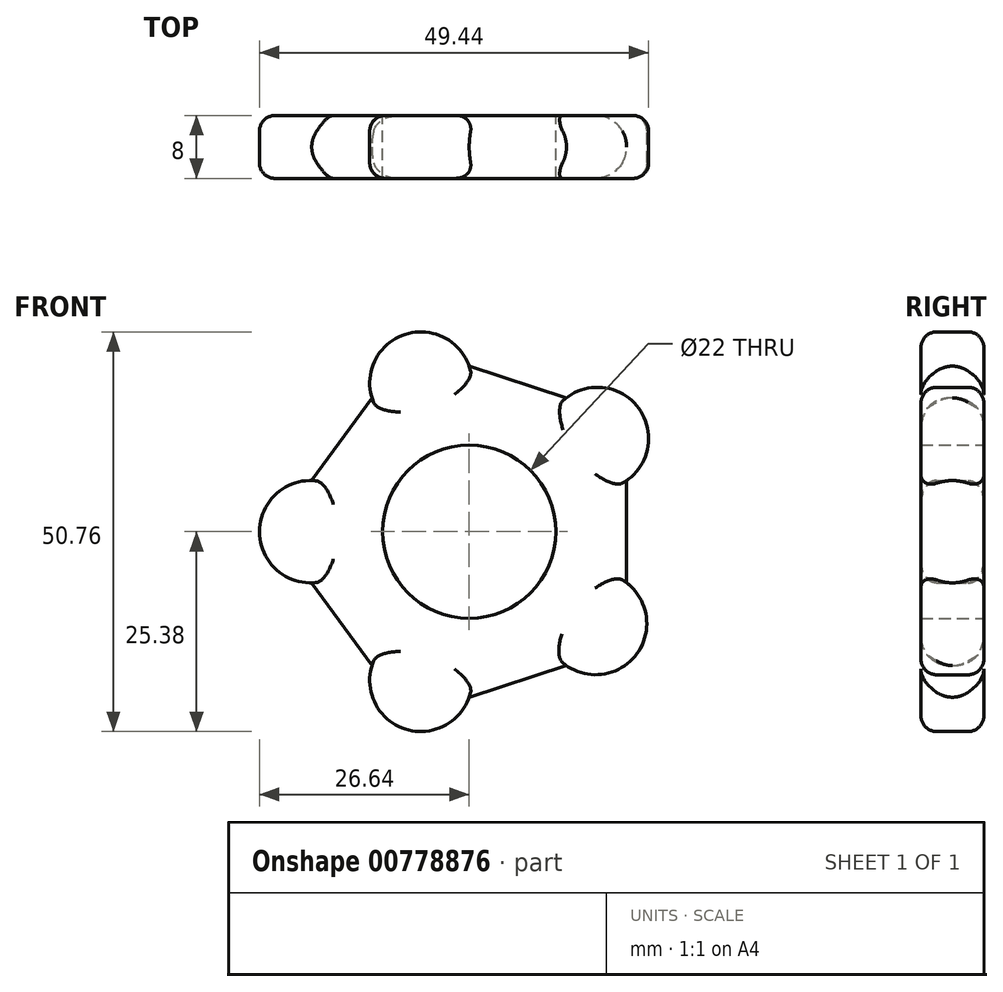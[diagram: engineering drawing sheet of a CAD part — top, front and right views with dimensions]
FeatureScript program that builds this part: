
annotation { "Feature Type Name" : "Feature", "Feature Type Description" : "" }
export const myFeature = defineFeature(function(context is Context, id is Id, definition is map)
    precondition{}
    {
        {
            var Q0;
            Q0=qCreatedBy(makeId("Front.planeOp"),FACE);
            var sketch = newSketch(context, id + "F0", { "sketchPlane" : qUnion([Q0])});
            skCircle(sketch, "E0.cCircle", {"center": v(0, 0) * mm, "radius": 20 * mm, "construction": true});
            skLineSegment(sketch, "E0.0", {"start": v(20, 6.5) * mm, "end": v(20, -6.5) * mm});
            skLineSegment(sketch, "E0.1", {"start": v(20, -6.5) * mm, "end": v(12.36, -17.01) * mm});
            skLineSegment(sketch, "E0.2", {"start": v(12.36, -17.01) * mm, "end": v(0, -21.03) * mm});
            skLineSegment(sketch, "E0.3", {"start": v(0, -21.03) * mm, "end": v(-12.36, -17.01) * mm});
            skLineSegment(sketch, "E0.4", {"start": v(-12.36, -17.01) * mm, "end": v(-20, -6.5) * mm});
            skLineSegment(sketch, "E0.5", {"start": v(-20, -6.5) * mm, "end": v(-20, 6.5) * mm});
            skLineSegment(sketch, "E0.6", {"start": v(-20, 6.5) * mm, "end": v(-12.36, 17.01) * mm});
            skLineSegment(sketch, "E0.7", {"start": v(-12.36, 17.01) * mm, "end": v(0, 21.03) * mm});
            skLineSegment(sketch, "E0.8", {"start": v(0, 21.03) * mm, "end": v(12.36, 17.01) * mm});
            skLineSegment(sketch, "E0.9", {"start": v(12.36, 17.01) * mm, "end": v(20, 6.5) * mm});
            skPoint(sketch, "E0.0.midPoint", {"position": v(20, 0) * mm});
            skCircle(sketch, "E1", {"center": v(0, 0) * mm, "radius": 11 * mm});
            skArc(sketch, "E2", {"start": v(20, 6.5) * mm, "mid": v(21.56, 15.66) * mm, "end": v(12.36, 17.01) * mm});
            skArc(sketch, "E3", {"start": v(12.36, -17.01) * mm, "mid": v(21.32, -15.5) * mm, "end": v(20, -6.5) * mm});
            skArc(sketch, "E4", {"start": v(-12.36, -17.01) * mm, "mid": v(-8.14, -25.07) * mm, "end": v(0, -21.03) * mm});
            skArc(sketch, "E5", {"start": v(-20, 6.5) * mm, "mid": v(-26.64, 0) * mm, "end": v(-20, -6.5) * mm});
            skArc(sketch, "E6", {"start": v(0, 21.03) * mm, "mid": v(-8.14, 25.07) * mm, "end": v(-12.36, 17.01) * mm});
            skSolve(sketch);
        }
        {
            var Q0;
            Q0=makeQuery(id+"F0.imprint","IMPRINT",FACE,{"disambiguationData":[TD([[makeQuery(id+"F0.imprint","IMPRINT",EDGE,{"derivedFrom":sQuery(id+"F0.wireOp",EDGE,"E0.0")}),-1.0]])]});
            var Q1;
            Q1=makeQuery(id+"F0.imprint","IMPRINT",FACE,{"disambiguationData":[TD([[makeQuery(id+"F0.imprint","IMPRINT",EDGE,{"derivedFrom":sQuery(id+"F0.wireOp",EDGE,"E0.1")}),1.0]])]});
            var Q2;
            Q2=makeQuery(id+"F0.imprint","IMPRINT",FACE,{"disambiguationData":[TD([[makeQuery(id+"F0.imprint","IMPRINT",EDGE,{"derivedFrom":sQuery(id+"F0.wireOp",EDGE,"E0.3")}),1.0]])]});
            var Q3;
            Q3=makeQuery(id+"F0.imprint","IMPRINT",FACE,{"disambiguationData":[TD([[makeQuery(id+"F0.imprint","IMPRINT",EDGE,{"derivedFrom":sQuery(id+"F0.wireOp",EDGE,"E0.5")}),1.0]])]});
            var Q4;
            {var subQ0=sQuery(id+"F0.wireOp",EDGE,"E0.7");Q4=makeQuery(id+"F0.imprint","IMPRINT",FACE,{"disambiguationData":[TD([[makeQuery(id+"F0.imprint","IMPRINT",EDGE,{"derivedFrom":subQ0}),1.0]])]});}
            var Q5;
            Q5=makeQuery(id+"F0.imprint","IMPRINT",FACE,{"disambiguationData":[TD([[makeQuery(id+"F0.imprint","IMPRINT",EDGE,{"derivedFrom":sQuery(id+"F0.wireOp",EDGE,"E0.9")}),1.0]])]});
            extrude(context, id + "F1", {"entities" : qUnion([Q0, Q1, Q2, Q3, Q4, Q5]), "depth" : 8 * mm, "offsetDistance" : 25 * mm});
        }
        {
            var Q0;
            Q0=makeQuery(id+"F1.opExtrude","CAP_EDGE",EDGE,{"disambiguationData":[OSD([sQuery(id+"F0.wireOp",EDGE,"E0.8")])],"isStart":false});
            var Q1;
            Q1=makeQuery(id+"F1.opExtrude","CAP_EDGE",EDGE,{"disambiguationData":[OSD([sQuery(id+"F0.wireOp",EDGE,"E0.0")])],"isStart":false});
            var Q2;
            Q2=makeQuery(id+"F1.opExtrude","CAP_EDGE",EDGE,{"disambiguationData":[OSD([sQuery(id+"F0.wireOp",EDGE,"E0.2")])],"isStart":false});
            var Q3;
            Q3=makeQuery(id+"F1.opExtrude","CAP_EDGE",EDGE,{"disambiguationData":[OSD([sQuery(id+"F0.wireOp",EDGE,"E0.4")])],"isStart":false});
            var Q4;
            Q4=makeQuery(id+"F1.opExtrude","CAP_EDGE",EDGE,{"disambiguationData":[OSD([sQuery(id+"F0.wireOp",EDGE,"E0.6")])],"isStart":false});
            var Q5;
            Q5=makeQuery(id+"F1.opExtrude","CAP_EDGE",EDGE,{"disambiguationData":[OSD([sQuery(id+"F0.wireOp",EDGE,"E0.2")])],"isStart":true});
            var Q6;
            Q6=makeQuery(id+"F1.opExtrude","CAP_EDGE",EDGE,{"disambiguationData":[OSD([sQuery(id+"F0.wireOp",EDGE,"E0.4")])],"isStart":true});
            var Q7;
            Q7=makeQuery(id+"F1.opExtrude","CAP_EDGE",EDGE,{"disambiguationData":[OSD([sQuery(id+"F0.wireOp",EDGE,"E0.0")])],"isStart":true});
            var Q8;
            Q8=makeQuery(id+"F1.opExtrude","CAP_EDGE",EDGE,{"disambiguationData":[OSD([sQuery(id+"F0.wireOp",EDGE,"E0.8")])],"isStart":true});
            var Q9;
            Q9=makeQuery(id+"F1.opExtrude","CAP_EDGE",EDGE,{"disambiguationData":[OSD([sQuery(id+"F0.wireOp",EDGE,"E0.6")])],"isStart":true});
            fillet(context, id + "F2", {"entities" : qUnion([Q0, Q1, Q2, Q3, Q4, Q5, Q6, Q7, Q8, Q9]), "radius" : 4 * mm, "tangentPropagation" : true, "allowEdgeOverflow" : false});
        }
        {
            var Q0;
            Q0=makeQuery(id+"F1.opExtrude","CAP_EDGE",EDGE,{"disambiguationData":[OSD([sQuery(id+"F0.wireOp",EDGE,"E3")])],"isStart":false});
            var Q1;
            Q1=makeQuery(id+"F1.opExtrude","CAP_EDGE",EDGE,{"disambiguationData":[OSD([sQuery(id+"F0.wireOp",EDGE,"E4")])],"isStart":false});
            var Q2;
            Q2=makeQuery(id+"F1.opExtrude","CAP_EDGE",EDGE,{"disambiguationData":[OSD([sQuery(id+"F0.wireOp",EDGE,"E5")])],"isStart":false});
            var Q3;
            Q3=makeQuery(id+"F1.opExtrude","CAP_EDGE",EDGE,{"disambiguationData":[OSD([sQuery(id+"F0.wireOp",EDGE,"E6")])],"isStart":false});
            var Q4;
            Q4=makeQuery(id+"F1.opExtrude","CAP_EDGE",EDGE,{"disambiguationData":[OSD([sQuery(id+"F0.wireOp",EDGE,"E2")])],"isStart":false});
            fillet(context, id + "F3", {"entities" : qUnion([Q0, Q1, Q2, Q3, Q4]), "radius" : 2 * mm, "tangentPropagation" : true, "allowEdgeOverflow" : false});
        }
        {
            var Q0;
            Q0=makeQuery(id+"F1.opExtrude","CAP_EDGE",EDGE,{"disambiguationData":[OSD([sQuery(id+"F0.wireOp",EDGE,"E6")])],"isStart":true});
            var Q1;
            Q1=makeQuery(id+"F1.opExtrude","CAP_EDGE",EDGE,{"disambiguationData":[OSD([sQuery(id+"F0.wireOp",EDGE,"E5")])],"isStart":true});
            var Q2;
            Q2=makeQuery(id+"F1.opExtrude","CAP_EDGE",EDGE,{"disambiguationData":[OSD([sQuery(id+"F0.wireOp",EDGE,"E4")])],"isStart":true});
            var Q3;
            Q3=makeQuery(id+"F1.opExtrude","CAP_EDGE",EDGE,{"disambiguationData":[OSD([sQuery(id+"F0.wireOp",EDGE,"E3")])],"isStart":true});
            var Q4;
            Q4=makeQuery(id+"F1.opExtrude","CAP_EDGE",EDGE,{"disambiguationData":[OSD([sQuery(id+"F0.wireOp",EDGE,"E2")])],"isStart":true});
            fillet(context, id + "F4", {"entities" : qUnion([Q0, Q1, Q2, Q3, Q4]), "radius" : 2 * mm, "tangentPropagation" : true, "allowEdgeOverflow" : false});
        }
    });
